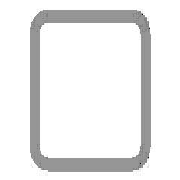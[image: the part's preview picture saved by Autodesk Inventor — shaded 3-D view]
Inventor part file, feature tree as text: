
AUTODESK INVENTOR PART (.ipt)
format: ipt  version: 2024 (Build 280153000, 153)  size: 135,168 bytes
history: native  units: mm (DEFAULTED — no unit token found)
features: other x4, plane x2, extrude x1, split x1, sketch x1
ambient origin geometry x8: Origin, YZ Plane, XZ Plane, XY Plane, X Axis, Y Axis, Z Axis, Center Point
bodies: Solid1 (feature_tree)
feature tree (9):
  parser-record x1  (decoder bookkeeping rows leaked as tree rows — omitted from the tree; the rows remain in map.json)
  other  "Driven Length"
  other  "Plano inicial"
  other  "Plano final"
  extrude  "Cuerpo"  TaperAngle=0.0deg  [1 undecoded]
  plane  "Plano de trabajo4"
  split  "Dividir1"
  sketch  "Sketch3"  dims[d3=2174.6mm d4=0.0mm d10=50.8mm d11=50.8mm d12=3.175mm d13=25.4mm d14=2200.0mm d15=25.4mm d16=25.4mm d17=6.35mm d18=90.0deg d19=2174.6mm]
  plane  "Work Plane3"
note: 1 required parameter value undecoded (feature->parameter linkage not recoverable at this tier; creation-order binding heuristic only, values carry confidence <= 0.55)
